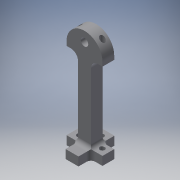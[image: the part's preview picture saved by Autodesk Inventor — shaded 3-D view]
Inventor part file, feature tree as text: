
AUTODESK INVENTOR PART (.ipt)
format: ipt  version: 2018 (Build 220112000, 112)  size: 236,544 bytes
history: native  units: mm
features: other x4, extrude x3, sketch x3, projected_geometry x3, fillet x2, reference x2
ambient origin geometry x8: Origin, YZ Plane, XZ Plane, XY Plane, X Axis, Y Axis, Z Axis, Center Point
bodies: Volumenkörper1 (feature_tree)
feature tree (17):
  extrude  "Extrusion1"  Depth=25.0mm
  extrude  "Extrusion2"  Depth=4.5mm
  extrude  "Extrusion3"  Depth=3.0mm
  fillet  "Rundung1"  Radius=75.0mm
  fillet  "Rundung2"  Radius=6.0mm
  sketch  "Skizze1"  dims[d0=9.0mm d1=25.0mm]
  reference  "Referenz1"
  sketch  "Skizze2"  dims[d2=4.5mm d3=4.5mm]
  projected_geometry  "Projizierte Kontur1"
  projected_geometry  "Projizierte Kontur2"
  sketch  "Skizze3"  dims[d4=25.0mm d5=8.0mm d6=75.0mm d7=0.0mm d8=6.0mm d9=75.0mm d10=0.0mm d12=75.0mm d13=0.0mm d14=5.2mm d15=5.0mm d16=3.0mm]
  projected_geometry  "Projizierte Kontur3"
  reference  "Referenz2"
  other  "<userpath>\OneDrive\Development\Mohne\03_Konstruktion\Mohne komplett.iam"
  other  "Mohne komplett.iam"
  other  "chassis mit motorlöcher:1"
  other  "Wheel ALL1_MIR:1"
